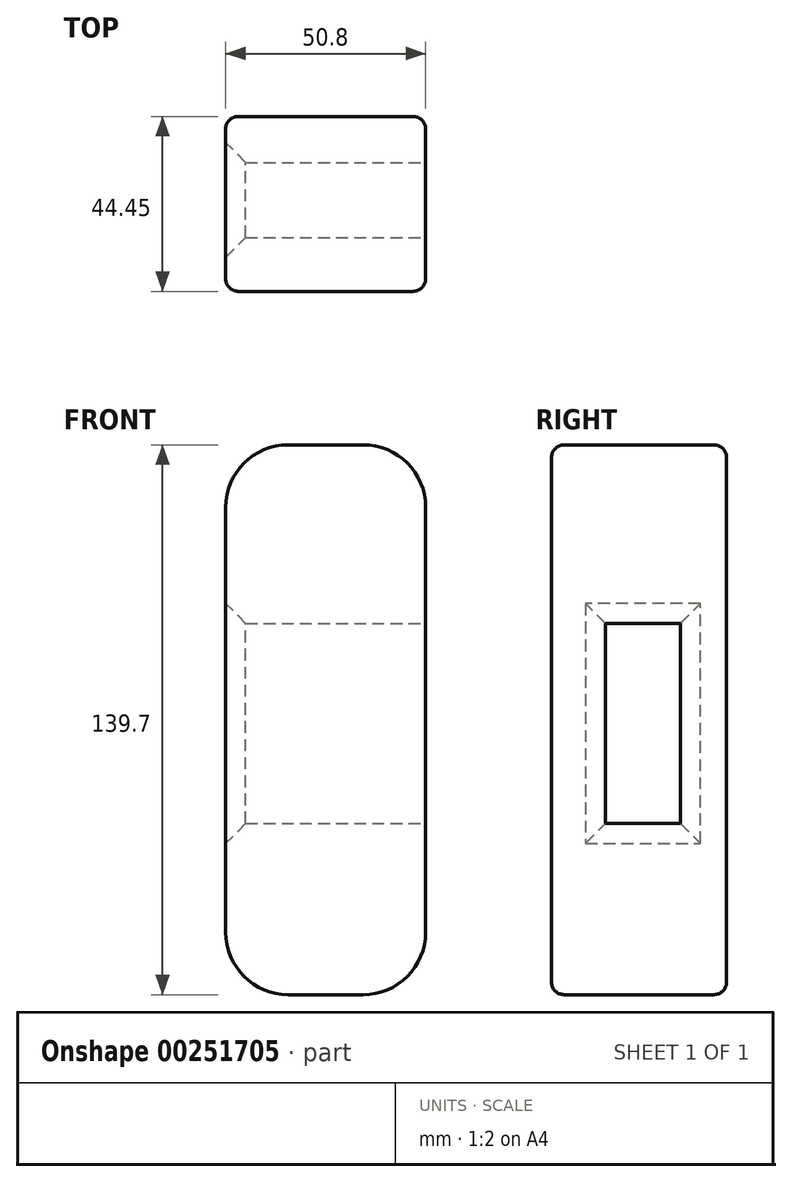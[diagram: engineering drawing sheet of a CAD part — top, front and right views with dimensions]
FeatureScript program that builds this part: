
annotation { "Feature Type Name" : "Feature", "Feature Type Description" : "" }
export const myFeature = defineFeature(function(context is Context, id is Id, definition is map)
    precondition{}
    {
        {
            var Q0;
            Q0=qCreatedBy(makeId("Front.planeOp"),FACE);
            var sketch = newSketch(context, id + "F0", { "sketchPlane" : qUnion([Q0])});
            skLineSegment(sketch, "E0.bottom", {"start": v(9.52, 69.85) * mm, "end": v(-9.53, 69.85) * mm});
            skLineSegment(sketch, "E0.top", {"start": v(9.53, -69.85) * mm, "end": v(-9.52, -69.85) * mm});
            skLineSegment(sketch, "E0.left", {"start": v(25.4, 53.98) * mm, "end": v(25.4, -53.97) * mm});
            skLineSegment(sketch, "E0.right", {"start": v(-25.4, 53.98) * mm, "end": v(-25.4, -53.98) * mm});
            skPoint(sketch, "E0.middle", {"position": v(0, 0) * mm});
            skPoint(sketch, "E1.visualSharp", {"position": v(-25.4, 69.85) * mm});
            skArc(sketch, "E1.filletArc", {"start": v(-9.53, 69.85) * mm, "mid": v(-20.75, 65.2) * mm, "end": v(-25.4, 53.98) * mm});
            skPoint(sketch, "E2.visualSharp", {"position": v(25.4, 69.85) * mm});
            skArc(sketch, "E2.filletArc", {"start": v(25.4, 53.98) * mm, "mid": v(20.75, 65.2) * mm, "end": v(9.52, 69.85) * mm});
            skPoint(sketch, "E3.visualSharp", {"position": v(-25.4, -69.85) * mm});
            skArc(sketch, "E3.filletArc", {"start": v(-25.4, -53.98) * mm, "mid": v(-20.75, -65.2) * mm, "end": v(-9.52, -69.85) * mm});
            skPoint(sketch, "E4.visualSharp", {"position": v(25.4, -69.85) * mm});
            skArc(sketch, "E4.filletArc", {"start": v(9.53, -69.85) * mm, "mid": v(20.75, -65.2) * mm, "end": v(25.4, -53.97) * mm});
            skSolve(sketch);
        }
        {
            var Q0;
            Q0 = qSketchRegion(id + "F0", true);
            extrude(context, id + "F1", {"entities" : qUnion([Q0]), "depth" : 44.45 * mm});
        }
        {
            var Q0;
            Q0=makeQuery(id+"F1.opExtrude","CAP_EDGE",EDGE,{"disambiguationData":[OSD([sQuery(id+"F0.wireOp",EDGE,"E0.right")])],"isStart":false});
            var Q1;
            Q1=makeQuery(id+"F1.opExtrude","CAP_EDGE",EDGE,{"disambiguationData":[OSD([sQuery(id+"F0.wireOp",EDGE,"E1.filletArc")])],"isStart":true});
            fillet(context, id + "F2", {"entities" : qUnion([Q0, Q1]), "radius" : 3.17 * mm, "tangentPropagation" : true, "allowEdgeOverflow" : false});
        }
        {
            var Q0;
            Q0=makeQuery(id+"F1.opExtrude","SWEPT_FACE",FACE,{"disambiguationData":[OSD([sQuery(id+"F0.wireOp",EDGE,"E0.left")])]});
            var sketch = newSketch(context, id + "F3", { "sketchPlane" : qUnion([Q0])});
            skLineSegment(sketch, "E5.bottom", {"start": v(-30.76, 24.46) * mm, "end": v(-11.7, 24.46) * mm});
            skLineSegment(sketch, "E5.top", {"start": v(-30.76, -26.34) * mm, "end": v(-11.7, -26.34) * mm});
            skLineSegment(sketch, "E5.left", {"start": v(-30.76, 24.46) * mm, "end": v(-30.76, -26.34) * mm});
            skLineSegment(sketch, "E5.right", {"start": v(-11.7, 24.46) * mm, "end": v(-11.7, -26.34) * mm});
            skSolve(sketch);
        }
        {
            var Q0;
            Q0 = qSketchRegion(id + "F3", true);
            extrude(context, id + "F4", {"entities" : qUnion([Q0]), "operationType" : NewBodyOperationType.REMOVE, "endBound" : BoundingType.THROUGH_ALL, "oppositeDirection" : true, "depth" : 25.4 * mm});
        }
        {
            var Q0;
            Q0=makeQuery(id+"F4.boolean.opBoolean","INTERSECT",EDGE,{"derivedFrom":[makeQuery(id+"F1.opExtrude","SWEPT_FACE",FACE,{"disambiguationData":[OSD([sQuery(id+"F0.wireOp",EDGE,"E0.right")])]}),makeQuery(id+"F4.opExtrude","SWEPT_FACE",FACE,{"disambiguationData":[OSD([sQuery(id+"F3.wireOp",EDGE,"E5.right")])]})]});
            var Q1;
            Q1=makeQuery(id+"F4.boolean.opBoolean","INTERSECT",EDGE,{"derivedFrom":[makeQuery(id+"F1.opExtrude","SWEPT_FACE",FACE,{"disambiguationData":[OSD([sQuery(id+"F0.wireOp",EDGE,"E0.right")])]}),makeQuery(id+"F4.opExtrude","SWEPT_FACE",FACE,{"disambiguationData":[OSD([sQuery(id+"F3.wireOp",EDGE,"E5.bottom")])]})]});
            var Q2;
            Q2=makeQuery(id+"F4.boolean.opBoolean","INTERSECT",EDGE,{"derivedFrom":[makeQuery(id+"F1.opExtrude","SWEPT_FACE",FACE,{"disambiguationData":[OSD([sQuery(id+"F0.wireOp",EDGE,"E0.right")])]}),makeQuery(id+"F4.opExtrude","SWEPT_FACE",FACE,{"disambiguationData":[OSD([sQuery(id+"F3.wireOp",EDGE,"E5.left")])]})]});
            var Q3;
            Q3=makeQuery(id+"F4.boolean.opBoolean","INTERSECT",EDGE,{"derivedFrom":[makeQuery(id+"F1.opExtrude","SWEPT_FACE",FACE,{"disambiguationData":[OSD([sQuery(id+"F0.wireOp",EDGE,"E0.right")])]}),makeQuery(id+"F4.opExtrude","SWEPT_FACE",FACE,{"disambiguationData":[OSD([sQuery(id+"F3.wireOp",EDGE,"E5.top")])]})]});
            var Q4;
            Q4=makeQuery(id+"F4.boolean.opBoolean","COPY",EDGE,{"derivedFrom":makeQuery(id+"F4.opExtrude","CAP_EDGE",EDGE,{"disambiguationData":[OSD([sQuery(id+"F3.wireOp",EDGE,"E5.bottom")])],"isStart":true})});
            var Q5;
            Q5=makeQuery(id+"F4.boolean.opBoolean","COPY",EDGE,{"derivedFrom":makeQuery(id+"F4.opExtrude","CAP_EDGE",EDGE,{"disambiguationData":[OSD([sQuery(id+"F3.wireOp",EDGE,"E5.right")])],"isStart":true})});
            var Q6;
            Q6=makeQuery(id+"F4.boolean.opBoolean","COPY",EDGE,{"derivedFrom":makeQuery(id+"F4.opExtrude","CAP_EDGE",EDGE,{"disambiguationData":[OSD([sQuery(id+"F3.wireOp",EDGE,"E5.top")])],"isStart":true})});
            var Q7;
            Q7=makeQuery(id+"F4.boolean.opBoolean","COPY",EDGE,{"derivedFrom":makeQuery(id+"F4.opExtrude","CAP_EDGE",EDGE,{"disambiguationData":[OSD([sQuery(id+"F3.wireOp",EDGE,"E5.left")])],"isStart":true})});
            chamfer(context, id + "F5", {"entities" : qUnion([Q0, Q1, Q2, Q3, Q4, Q5, Q6, Q7]), "width" : 5.08 * mm, "tangentPropagation" : true});
        }
    });
